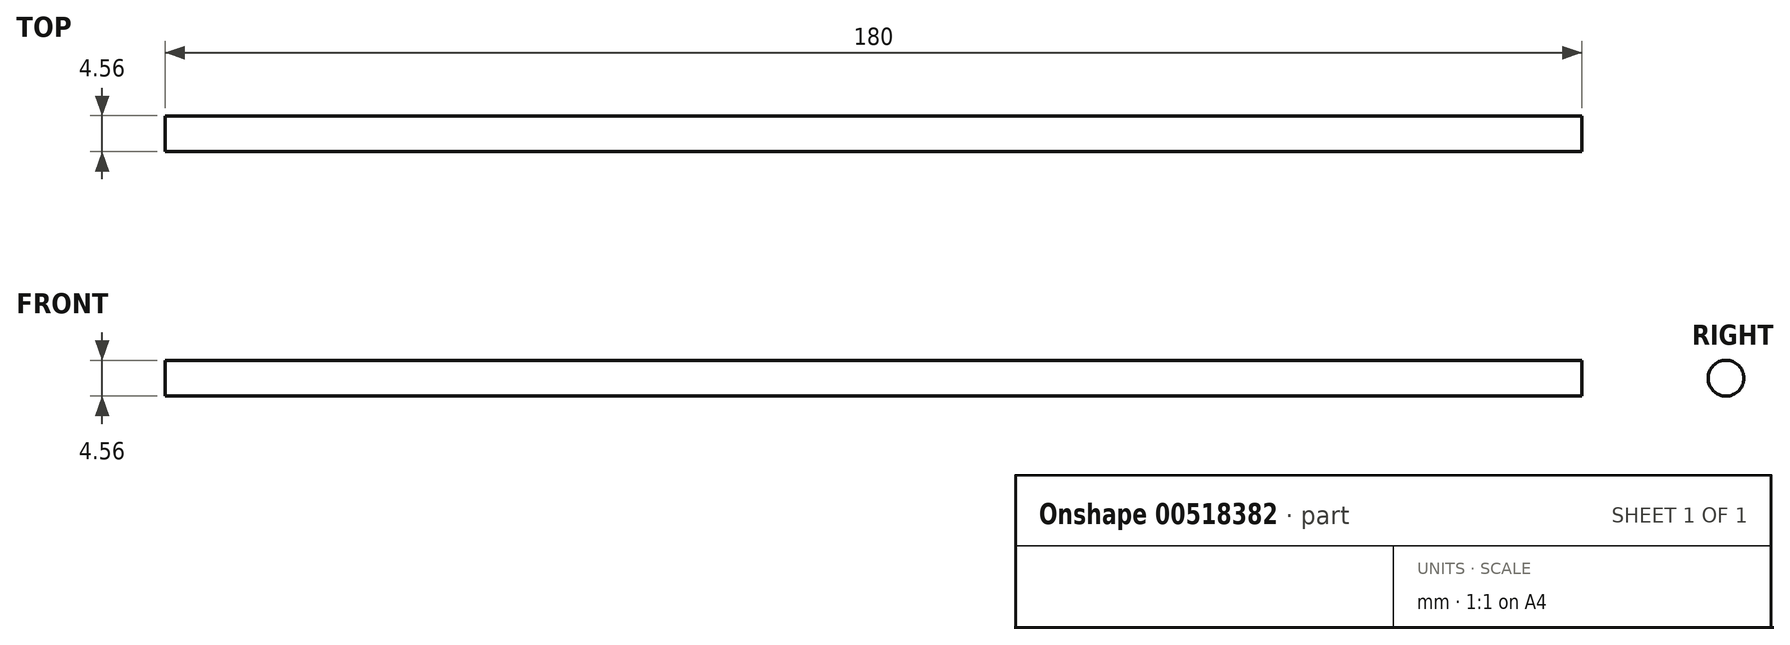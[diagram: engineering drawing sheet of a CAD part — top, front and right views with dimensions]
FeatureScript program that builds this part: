
annotation { "Feature Type Name" : "Feature", "Feature Type Description" : "" }
export const myFeature = defineFeature(function(context is Context, id is Id, definition is map)
    precondition{}
    {
        {
            var Q0;
            Q0=qCreatedBy(makeId("Right.planeOp"),FACE);
            var sketch = newSketch(context, id + "F0", { "sketchPlane" : qUnion([Q0])});
            skCircle(sketch, "E0", {"center": v(0, 0) * mm, "radius": 2.27 * mm});
            skSolve(sketch);
        }
        {
            var Q0;
            Q0=qSketchRegion(id+"F0",true);
            extrude(context, id + "F1", {"entities" : qUnion([Q0]), "depth" : 180 * mm, "offsetDistance" : 25 * mm});
        }
    });
